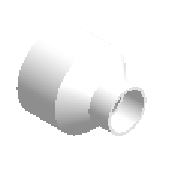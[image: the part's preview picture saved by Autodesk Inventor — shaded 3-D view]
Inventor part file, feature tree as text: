
AUTODESK INVENTOR PART (.ipt)
format: ipt  version: 2023 (Build 270158000, 158)  size: 169,472 bytes
history: native  units: mm (DEFAULTED — no unit token found)
features: other x6, revolve x1, sketch x1
ambient origin geometry x8: Origin, YZ Plane, XZ Plane, XY Plane, X Axis, Y Axis, Z Axis, Center Point
bodies: Solid1 (feature_tree)
feature tree (8):
  revolve  "Revolve1"  [1 undecoded]
  other  "Work Point1"
  other  "Work Point2"
  other  "Work Axis1"
  other  "Work Point3"
  other  "Work Axis2"
  other  "Work Point4"
  sketch  "Sketch1"  dims[d0=6.7mm d1=13.4mm d2=8.2mm d3=55.0mm d4=45.0mm d5=51.0mm d6=61.0mm d7=88.0mm d9=90.0deg]
note: 1 required parameter value undecoded (feature->parameter linkage not recoverable at this tier; creation-order binding heuristic only, values carry confidence <= 0.55)
